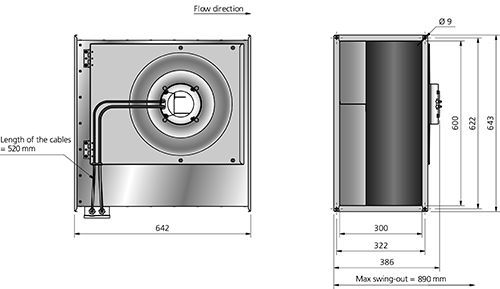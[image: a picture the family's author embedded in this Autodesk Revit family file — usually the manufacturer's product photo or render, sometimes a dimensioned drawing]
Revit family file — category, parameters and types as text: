
# Revit family: RKB 600X300 B1 EC_7480101
name_source: partatom
category: Mechanical Equipment
revit_build: Autodesk Revit MEP 2014 (Build: 20130308_1515(x64)
units: mm (PartAtom-declared; Revit-internal decimal feet)

## types (1)
- RKB 600X300 B1 EC
    Capacitor = - μF
    Connector Height = 300 mm
    Connector Width = 600 mm
    Current = 4 A
    Depth = 643 mm  [stored 2.10958 ft]
    Description = UNINSULATED DUCT FANS WITH RECTANGULAR CONNECTIONS
    Frequency = 50 Hz
    Height = 391 mm
    Main Material = Steel, Galvanized
    Max. temperature of transported air = 60 °C
    Max. temperature of transported air when speed controlled = 60 °C
    Phase = 1
    Power = 868 W
    Sound pressure level at 3 m = 67 dB(A)
    Speed = 2190 rpm
    Voltage = 230 V
    Voltage range = 200-277 V
    Weight = 29.20 kg
    Width = 642 mm  [stored 2.1063 ft]
    Wiring diagram = 4040145

note: [stored X ft] marks values corroborated as IEEE doubles in the binary element streams (Revit-internal decimal feet)

## geometry (parser evidence)
native form markers: Sweep x4
no freeform markers — native parametric forms only
